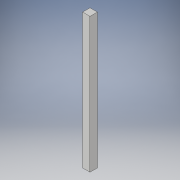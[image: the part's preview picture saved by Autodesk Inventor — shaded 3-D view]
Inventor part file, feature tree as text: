
AUTODESK INVENTOR PART (.ipt)
format: ipt  version: 2017 (Build 210142000, 142)  size: 91,136 bytes
history: native  units: in
note: dims shown in document units (in); Inventor stores cm internally (conversion verified against a paired STEP export)
features: extrude x1, sketch x1
ambient origin geometry x8: Origin, YZ Plane, XZ Plane, XY Plane, X Axis, Y Axis, Z Axis, Center Point
bodies: Solid1 (feature_tree)
feature tree (2):
  extrude  "Extrusion1"  Depth=3.0in
  sketch  "Sketch1"  dims[d0=3.0in d1=3.0in d2=55.0in d3=0.0in]
